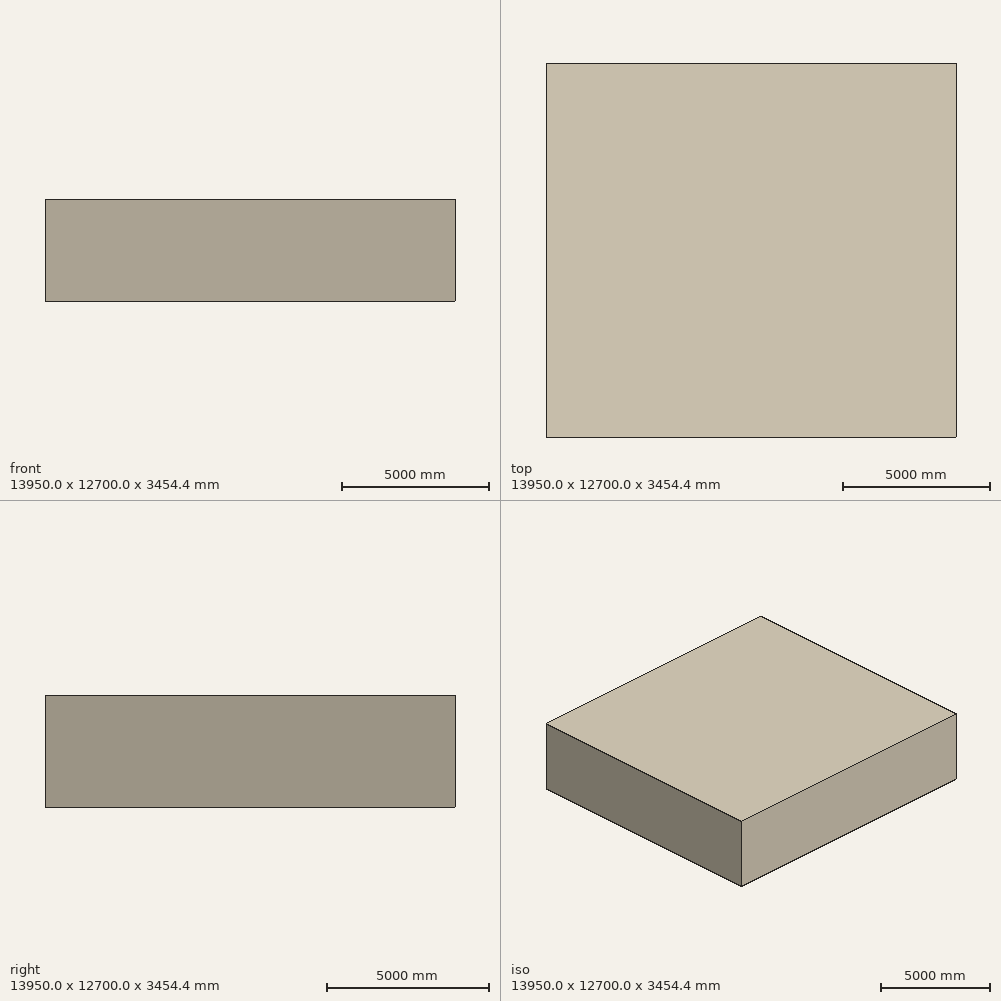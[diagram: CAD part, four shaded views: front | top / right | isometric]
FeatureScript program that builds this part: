
annotation { "Feature Type Name" : "Feature", "Feature Type Description" : "" }
export const myFeature = defineFeature(function(context is Context, id is Id, definition is map)
    precondition{}
    {
        {
            var Q0;
            Q0=qCreatedBy(makeId("Top.planeOp"),FACE);
            var sketch = newSketch(context, id + "F0", { "sketchPlane" : qUnion([Q0])});
            skLineSegment(sketch, "E0.bottom", {"start": v(-13950, 12700) * mm, "end": v(0, 12700) * mm});
            skLineSegment(sketch, "E0.top", {"start": v(-13950, 0) * mm, "end": v(0, 0) * mm});
            skLineSegment(sketch, "E0.left", {"start": v(-13950, 12700) * mm, "end": v(-13950, 0) * mm});
            skLineSegment(sketch, "E0.right", {"start": v(0, 12700) * mm, "end": v(0, 0) * mm});
            skSolve(sketch);
        }
        {
            var Q0;
            Q0=makeQuery(id+"F0.imprint","IMPRINT",FACE,{"disambiguationData":[TD([[makeQuery(id+"F0.imprint","IMPRINT",EDGE,{"derivedFrom":sQuery(id+"F0.wireOp",EDGE,"E0.bottom")}),-1.0]])]});
            extrude(context, id + "F1", {"entities" : qUnion([Q0]), "depth" : 3454.4 * mm, "offsetDistance" : 25.4 * mm});
        }
    });
